# Revit family: Window_Detention
name_source: partatom
category: Windows
units: mm (PartAtom-declared; Revit-internal decimal feet)

## family parameters
Always vertical = Yes
Classification Number = 23.30.20.24.11
Cut with Voids When Loaded = No
Host = Wall
Room Calculation Point = No
Shared = No

## types (1)
- Custom Sizing
    Air Infiltration = 0.20 CFM at 1.57 PSF
    Assembly Code = B2020120
    Bar Width = 0' - 1"
    Cladding Material = ARCAT - Metal - Brass - BHMA606 - Dull Brass
    Construction Details = http://www.arcat.com
    Default Sill Height = 3' - 6"
    Description = Detention Window
    Expected Lifespan (Years) = 10
    Exterior Security Frame Depth = 0' - 1"
    Fastening = Exterior Mounted, Tamper and Corrosion Resistant Expansion Bolts
    Glass Thickness = 0' - 0 7/8"
    Green Building-LEED = http://www.arcat.com
    Height = 3' - 0"
    Impact Resistance = Tested in accorance with ASTM F 1592
    Interior Casing Width = 0' - 4"
    Keynote = 08580
    Maintenance Schedule (Months) = 6
    Manufacturer = Generic
    Manufacturer Fax = (203) 929-2444
    Model = Generic
    Product Data = http://www.arcat.com
    Product Properties = http://www.arcat.com
    Rough Height = 3' - 1 1/2"
    Rough Width = 4' - 5 1/2"
    SHGC = 0.49
    Security Frame Material = ARCAT - Metal - Steel 1/4" - Painted - Black
    Sound Transmission Class (STC) = 42
    Specification = http://www.arcat.com
    U-Factor = 0.4
    Wall Closure = By host
    Warranty Duration (Years) = 2
    Water Penetration = Lo leakage at 2.86 PSF
    Width = 4' - 4"
    Window Frame Material = ARCAT - Metal - Steel 18ga - Painted - Green

## geometry (parser evidence)
native form markers: Blend x3, Sweep x4
no freeform markers — native parametric forms only
